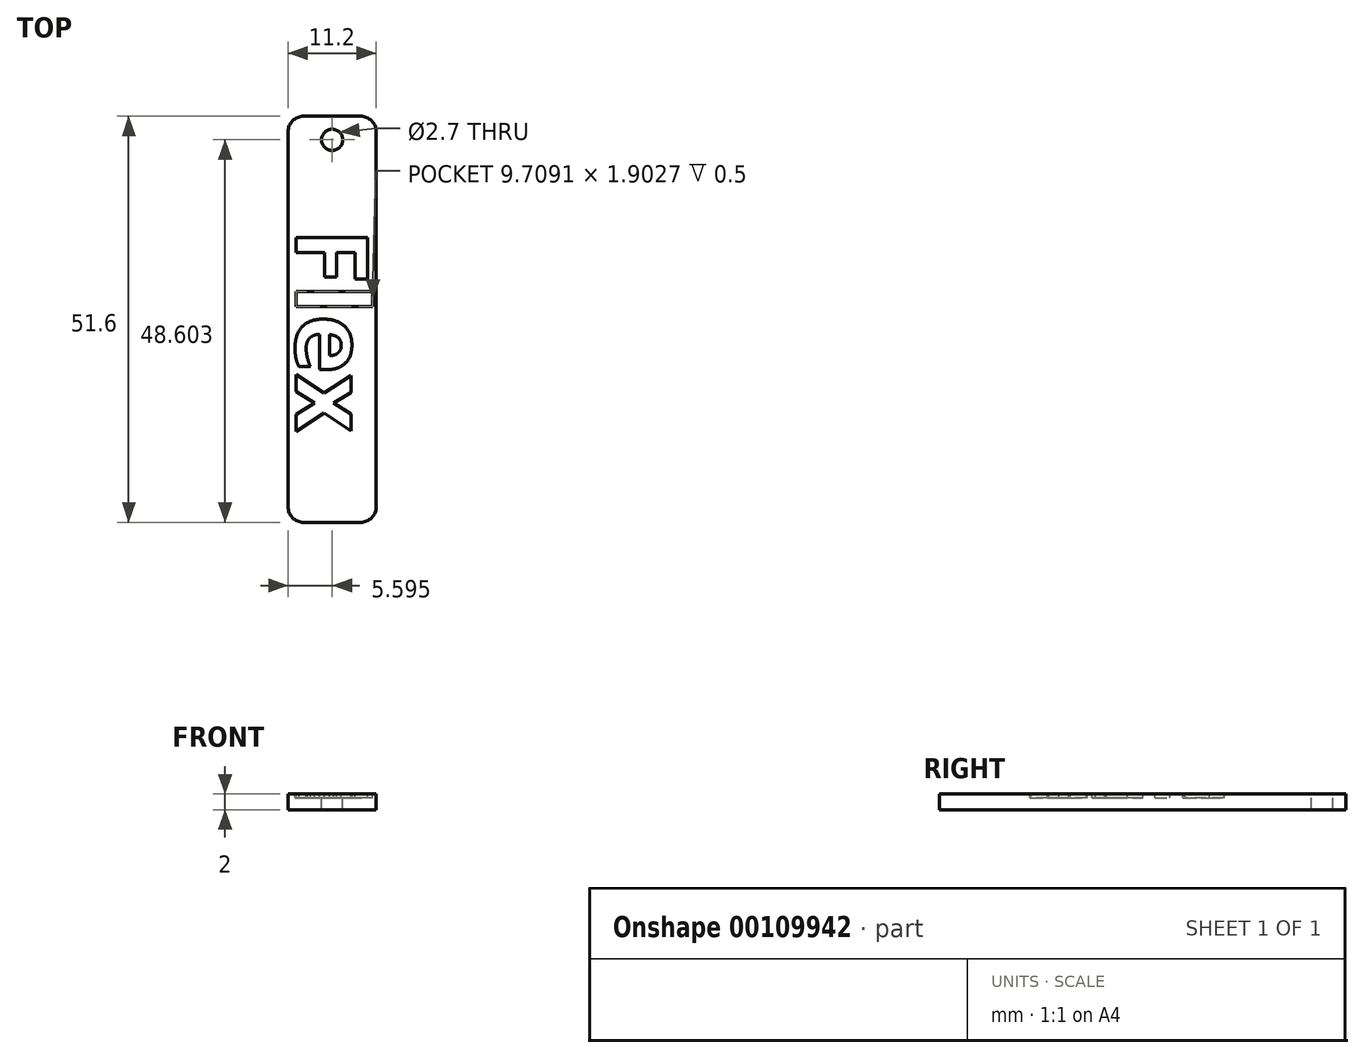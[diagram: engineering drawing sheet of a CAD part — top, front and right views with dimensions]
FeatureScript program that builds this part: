
annotation { "Feature Type Name" : "Feature", "Feature Type Description" : "" }
export const myFeature = defineFeature(function(context is Context, id is Id, definition is map)
    precondition{}
    {
        {
            var Q0;
            Q0=qCreatedBy(makeId("Top.planeOp"),FACE);
            var sketch = newSketch(context, id + "F0", { "sketchPlane" : qUnion([Q0])});
            skLineSegment(sketch, "E0.bottom", {"start": v(-49.26, 79.43) * mm, "end": v(-38.06, 79.43) * mm});
            skLineSegment(sketch, "E0.top", {"start": v(-49.26, 27.83) * mm, "end": v(-38.06, 27.83) * mm});
            skLineSegment(sketch, "E0.left", {"start": v(-49.26, 79.43) * mm, "end": v(-49.26, 27.83) * mm});
            skLineSegment(sketch, "E0.right", {"start": v(-38.06, 79.43) * mm, "end": v(-38.06, 27.83) * mm});
            skCircle(sketch, "E1", {"center": v(-43.66, 76.43) * mm, "radius": 1.35 * mm});
            skText(sketch, "E2", { "text": "Flex", "fontName": "OpenSans-Bold.ttf"});
            const initialGuessF0  = {"E2": [-0.04826, 0.06514, 0, -1, 0.0092]};
            skSetInitialGuess(sketch, initialGuessF0);
            skSolve(sketch);
        }
        {
            var Q0;
            Q0=makeQuery(id+"F0.imprint","IMPRINT",FACE,{"disambiguationData":[TD([[makeQuery(id+"F0.imprint","IMPRINT",EDGE,{"derivedFrom":sQuery(id+"F0.wireOp",EDGE,"E2.sketch_text.stroke-8")}),1.0]])]});
            var Q1;
            Q1=makeQuery(id+"F0.imprint","IMPRINT",FACE,{"disambiguationData":[TD([[makeQuery(id+"F0.imprint","IMPRINT",EDGE,{"derivedFrom":sQuery(id+"F0.wireOp",EDGE,"E2.sketch_text.stroke-14")}),-1.0]])]});
            var Q2;
            Q2=makeQuery(id+"F0.imprint","IMPRINT",FACE,{"disambiguationData":[TD([[makeQuery(id+"F0.imprint","IMPRINT",EDGE,{"derivedFrom":sQuery(id+"F0.wireOp",EDGE,"E2.sketch_text.stroke-32")}),-1.0]])]});
            var Q3;
            Q3=makeQuery(id+"F0.imprint","IMPRINT",FACE,{"disambiguationData":[TD([[makeQuery(id+"F0.imprint","IMPRINT",EDGE,{"derivedFrom":sQuery(id+"F0.wireOp",EDGE,"E2.sketch_text.stroke-49")}),-1.0]])]});
            var Q4;
            Q4=makeQuery(id+"F0.imprint","IMPRINT",FACE,{"disambiguationData":[TD([[makeQuery(id+"F0.imprint","IMPRINT",EDGE,{"derivedFrom":sQuery(id+"F0.wireOp",EDGE,"E2.sketch_text.stroke-69")}),-1.0]])]});
            var Q5;
            Q5=makeQuery(id+"F0.imprint","IMPRINT",FACE,{"disambiguationData":[TD([[makeQuery(id+"F0.imprint","IMPRINT",EDGE,{"derivedFrom":sQuery(id+"F0.wireOp",EDGE,"E0.bottom")}),-1.0]])]});
            var Q6;
            Q6=makeQuery(id+"F0.imprint","IMPRINT",FACE,{"disambiguationData":[TD([[makeQuery(id+"F0.imprint","IMPRINT",EDGE,{"derivedFrom":sQuery(id+"F0.wireOp",EDGE,"E2.sketch_text.stroke-0")}),-1.0]])]});
            var Q7;
            Q7=makeQuery(id+"F0.imprint","IMPRINT",FACE,{"disambiguationData":[TD([[makeQuery(id+"F0.imprint","IMPRINT",EDGE,{"derivedFrom":sQuery(id+"F0.wireOp",EDGE,"E2.sketch_text.stroke-49")}),1.0]])]});
            var Q8;
            Q8=makeQuery(id+"F0.imprint","IMPRINT",FACE,{"disambiguationData":[TD([[makeQuery(id+"F0.imprint","IMPRINT",EDGE,{"derivedFrom":sQuery(id+"F0.wireOp",EDGE,"E2.sketch_text.stroke-10")}),-1.0]])]});
            var Q9;
            Q9=makeQuery(id+"F0.imprint","IMPRINT",FACE,{"disambiguationData":[TD([[makeQuery(id+"F0.imprint","IMPRINT",EDGE,{"derivedFrom":sQuery(id+"F0.wireOp",EDGE,"E2.sketch_text.stroke-14")}),1.0]])]});
            var Q10;
            Q10=makeQuery(id+"F0.imprint","IMPRINT",FACE,{"disambiguationData":[TD([[makeQuery(id+"F0.imprint","IMPRINT",EDGE,{"derivedFrom":sQuery(id+"F0.wireOp",EDGE,"E2.sketch_text.stroke-34")}),-1.0]])]});
            extrude(context, id + "F1", {"entities" : qUnion([Q0, Q1, Q2, Q3, Q4, Q5, Q6, Q7, Q8, Q9, Q10]), "oppositeDirection" : true, "depth" : 2 * mm});
        }
        {
            var Q0;
            Q0=makeQuery(id+"F0.imprint","IMPRINT",FACE,{"disambiguationData":[TD([[makeQuery(id+"F0.imprint","IMPRINT",EDGE,{"derivedFrom":sQuery(id+"F0.wireOp",EDGE,"E2.sketch_text.stroke-0")}),-1.0]])]});
            var Q1;
            Q1=makeQuery(id+"F0.imprint","IMPRINT",FACE,{"disambiguationData":[TD([[makeQuery(id+"F0.imprint","IMPRINT",EDGE,{"derivedFrom":sQuery(id+"F0.wireOp",EDGE,"E2.sketch_text.stroke-16")}),-1.0]])]});
            var Q2;
            Q2=makeQuery(id+"F0.imprint","IMPRINT",FACE,{"disambiguationData":[TD([[makeQuery(id+"F0.imprint","IMPRINT",EDGE,{"derivedFrom":sQuery(id+"F0.wireOp",EDGE,"E2.sketch_text.stroke-28")}),-1.0]])]});
            var Q3;
            Q3=makeQuery(id+"F0.imprint","IMPRINT",FACE,{"disambiguationData":[TD([[makeQuery(id+"F0.imprint","IMPRINT",EDGE,{"derivedFrom":sQuery(id+"F0.wireOp",EDGE,"E2.sketch_text.stroke-36")}),-1.0]])]});
            var Q4;
            Q4=makeQuery(id+"F0.imprint","IMPRINT",FACE,{"disambiguationData":[TD([[makeQuery(id+"F0.imprint","IMPRINT",EDGE,{"derivedFrom":sQuery(id+"F0.wireOp",EDGE,"E2.sketch_text.stroke-49")}),-1.0]])]});
            var Q5;
            Q5=makeQuery(id+"F0.imprint","IMPRINT",FACE,{"disambiguationData":[TD([[makeQuery(id+"F0.imprint","IMPRINT",EDGE,{"derivedFrom":sQuery(id+"F0.wireOp",EDGE,"E2.sketch_text.stroke-69")}),-1.0]])]});
            var Q6;
            Q6=makeQuery(id+"F0.imprint","IMPRINT",FACE,{"disambiguationData":[TD([[makeQuery(id+"F0.imprint","IMPRINT",EDGE,{"derivedFrom":sQuery(id+"F0.wireOp",EDGE,"E2.sketch_text.stroke-10")}),-1.0]])]});
            var Q7;
            Q7=qConstructionFilter(qBodyType(qCreatedBy(id+"F0",EDGE),BodyType.WIRE),ConstructionObject.NO);
            extrude(context, id + "F2", {"entities" : qUnion([Q0, Q1, Q2, Q3, Q4, Q5, Q6]), "operationType" : NewBodyOperationType.REMOVE, "surfaceEntities" : qUnion([Q7]), "oppositeDirection" : true, "depth" : .5 * mm});
        }
        {
            var Q0;
            Q0=makeQuery(id+"F1.opExtrude","SWEPT_EDGE",EDGE,{"disambiguationData":[OSD([sQuery(id+"F0.wireOp",EDGE,"E0.bottom"),sQuery(id+"F0.wireOp",EDGE,"E0.left")])]});
            var Q1;
            Q1=makeQuery(id+"F1.opExtrude","SWEPT_EDGE",EDGE,{"disambiguationData":[OSD([sQuery(id+"F0.wireOp",EDGE,"E0.bottom"),sQuery(id+"F0.wireOp",EDGE,"E0.right")])]});
            var Q2;
            Q2=makeQuery(id+"F1.opExtrude","SWEPT_EDGE",EDGE,{"disambiguationData":[OSD([sQuery(id+"F0.wireOp",EDGE,"E0.top"),sQuery(id+"F0.wireOp",EDGE,"E0.right")])]});
            var Q3;
            Q3=makeQuery(id+"F1.opExtrude","SWEPT_EDGE",EDGE,{"disambiguationData":[OSD([sQuery(id+"F0.wireOp",EDGE,"E0.top"),sQuery(id+"F0.wireOp",EDGE,"E0.left")])]});
            fillet(context, id + "F3", {"entities" : qUnion([Q0, Q1, Q2, Q3]), "radius" : 2 * mm, "tangentPropagation" : true, "allowEdgeOverflow" : false});
        }
    });
